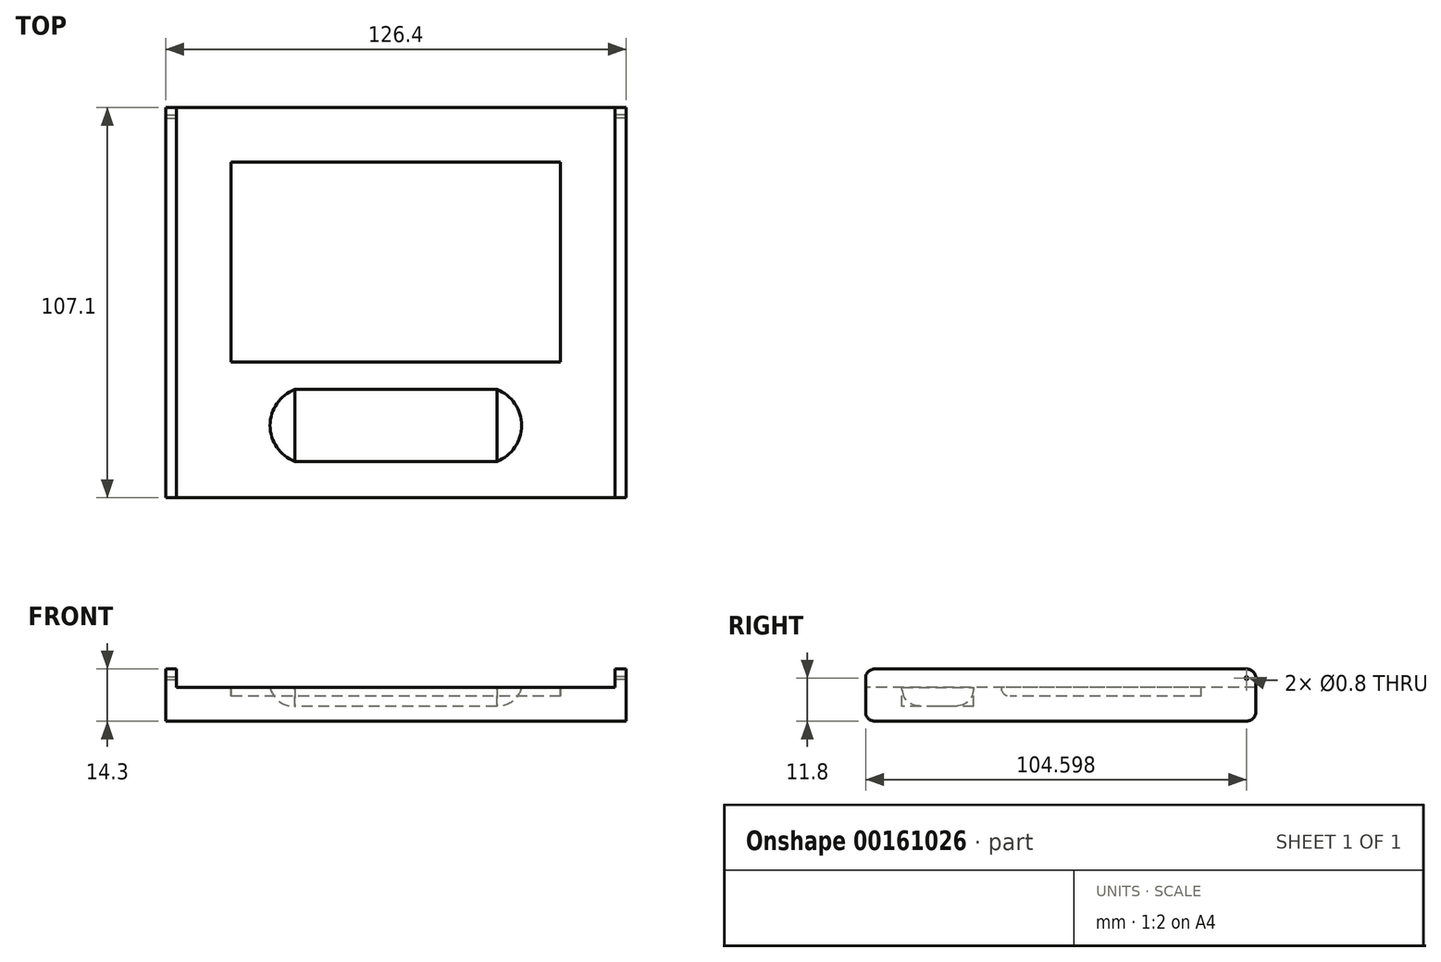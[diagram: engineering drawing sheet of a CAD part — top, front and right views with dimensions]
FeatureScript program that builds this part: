
annotation { "Feature Type Name" : "Feature", "Feature Type Description" : "" }
export const myFeature = defineFeature(function(context is Context, id is Id, definition is map)
    precondition{}
    {
        {
            var Q0;
            Q0=qCreatedBy(makeId("Top.planeOp"),FACE);
            var sketch = newSketch(context, id + "F0", { "sketchPlane" : qUnion([Q0])});
            skLineSegment(sketch, "E0", {"start": v(0, 49.02) * mm, "end": v(0, -3.38) * mm, "construction": true});
            skLineSegment(sketch, "E1.bottom", {"start": v(0, 49.02) * mm, "end": v(-45.2, 49.02) * mm});
            skLineSegment(sketch, "E1.top", {"start": v(0, -3.38) * mm, "end": v(-45.2, -3.38) * mm});
            skLineSegment(sketch, "E1.right", {"start": v(-45.2, 49.02) * mm, "end": v(-45.2, -3.38) * mm});
            skLineSegment(sketch, "E2.bottom", {"start": v(0, -13.38) * mm, "end": v(-27.75, -13.38) * mm});
            skLineSegment(sketch, "E2.top", {"start": v(-0.7, -33.08) * mm, "end": v(-27.75, -33.08) * mm});
            skLineSegment(sketch, "E2.right", {"start": v(-27.75, -13.38) * mm, "end": v(-27.75, -33.08) * mm});
            skLineSegment(sketch, "E3.bottom", {"start": v(0, 64.02) * mm, "end": v(-60.2, 64.02) * mm});
            skLineSegment(sketch, "E3.top", {"start": v(-0.7, -43.08) * mm, "end": v(-60.2, -43.08) * mm});
            skLineSegment(sketch, "E3.right", {"start": v(-60.2, 64.02) * mm, "end": v(-60.2, -43.08) * mm});
            skLineSegment(sketch, "E4.MirrorCS", {"start": v(-0.7, -43.08) * mm, "end": v(60.2, -43.08) * mm});
            skLineSegment(sketch, "E5.MirrorCS", {"start": v(-0.7, -33.08) * mm, "end": v(27.75, -33.08) * mm});
            skLineSegment(sketch, "E6.MirrorCS", {"start": v(27.75, -13.38) * mm, "end": v(27.75, -33.08) * mm});
            skLineSegment(sketch, "E7.MirrorCS", {"start": v(0, -13.38) * mm, "end": v(27.75, -13.38) * mm});
            skLineSegment(sketch, "E8.MirrorCS", {"start": v(0, -3.38) * mm, "end": v(45.2, -3.38) * mm});
            skLineSegment(sketch, "E9.MirrorCS", {"start": v(60.2, 64.02) * mm, "end": v(60.2, -43.08) * mm});
            skLineSegment(sketch, "E10.MirrorCS", {"start": v(45.2, 49.02) * mm, "end": v(45.2, -3.38) * mm});
            skLineSegment(sketch, "E11.MirrorCS", {"start": v(0, 64.02) * mm, "end": v(60.2, 64.02) * mm});
            skLineSegment(sketch, "E12.MirrorCS", {"start": v(0, 49.02) * mm, "end": v(45.2, 49.02) * mm});
            skLineSegment(sketch, "E13", {"start": v(-60.2, 64.02) * mm, "end": v(-63.2, 64.02) * mm});
            skLineSegment(sketch, "E14", {"start": v(-63.2, 64.02) * mm, "end": v(-63.2, -43.08) * mm});
            skLineSegment(sketch, "E15", {"start": v(-63.2, -43.08) * mm, "end": v(-60.2, -43.08) * mm});
            skLineSegment(sketch, "E16.MirrorCS", {"start": v(63.2, -43.08) * mm, "end": v(60.2, -43.08) * mm});
            skLineSegment(sketch, "E17.MirrorCS", {"start": v(63.2, 64.02) * mm, "end": v(63.2, -43.08) * mm});
            skLineSegment(sketch, "E18.MirrorCS", {"start": v(60.2, 64.02) * mm, "end": v(63.2, 64.02) * mm});
            skPoint(sketch, "E19.orphan", {"position": v(0.7, -33.08) * mm});
            skPoint(sketch, "E20.orphan", {"position": v(0.7, -43.08) * mm});
            skSolve(sketch);
        }
        {
            var Q0;
            Q0=makeQuery(id+"F0.imprint","IMPRINT",FACE,{"disambiguationData":[TD([[makeQuery(id+"F0.imprint","IMPRINT",EDGE,{"derivedFrom":sQuery(id+"F0.wireOp",EDGE,"E2.bottom")}),1.0]])]});
            var Q1;
            Q1=makeQuery(id+"F0.imprint","IMPRINT",FACE,{"disambiguationData":[TD([[makeQuery(id+"F0.imprint","IMPRINT",EDGE,{"derivedFrom":sQuery(id+"F0.wireOp",EDGE,"E1.bottom")}),1.0]])]});
            var Q2;
            Q2=makeQuery(id+"F0.imprint","IMPRINT",FACE,{"disambiguationData":[TD([[makeQuery(id+"F0.imprint","IMPRINT",EDGE,{"derivedFrom":sQuery(id+"F0.wireOp",EDGE,"E1.bottom")}),-1.0]])]});
            var Q3;
            Q3=makeQuery(id+"F0.imprint","IMPRINT",FACE,{"disambiguationData":[TD([[makeQuery(id+"F0.imprint","IMPRINT",EDGE,{"derivedFrom":sQuery(id+"F0.wireOp",EDGE,"E3.right")}),-1.0]])]});
            var Q4;
            Q4=makeQuery(id+"F0.imprint","IMPRINT",FACE,{"disambiguationData":[TD([[makeQuery(id+"F0.imprint","IMPRINT",EDGE,{"derivedFrom":sQuery(id+"F0.wireOp",EDGE,"E9.MirrorCS")}),1.0]])]});
            extrude(context, id + "F1", {"entities" : qUnion([Q0, Q1, Q2, Q3, Q4]), "oppositeDirection" : true, "depth" : (5 + 6.3 + 3) * mm});
        }
        {
            var Q0;
            Q0=makeQuery(id+"F0.imprint","IMPRINT",FACE,{"disambiguationData":[TD([[makeQuery(id+"F0.imprint","IMPRINT",EDGE,{"derivedFrom":sQuery(id+"F0.wireOp",EDGE,"E1.bottom")}),-1.0]])]});
            var Q1;
            Q1=makeQuery(id+"F0.imprint","IMPRINT",FACE,{"disambiguationData":[TD([[makeQuery(id+"F0.imprint","IMPRINT",EDGE,{"derivedFrom":sQuery(id+"F0.wireOp",EDGE,"E1.bottom")}),1.0]])]});
            var Q2;
            Q2=makeQuery(id+"F0.imprint","IMPRINT",FACE,{"disambiguationData":[TD([[makeQuery(id+"F0.imprint","IMPRINT",EDGE,{"derivedFrom":sQuery(id+"F0.wireOp",EDGE,"E2.bottom")}),1.0]])]});
            extrude(context, id + "F2", {"entities" : qUnion([Q0, Q1, Q2]), "operationType" : NewBodyOperationType.REMOVE, "oppositeDirection" : true, "depth" : 5 * mm});
        }
        {
            var Q0;
            Q0=makeQuery(id+"F0.imprint","IMPRINT",FACE,{"disambiguationData":[TD([[makeQuery(id+"F0.imprint","IMPRINT",EDGE,{"derivedFrom":sQuery(id+"F0.wireOp",EDGE,"E1.bottom")}),1.0]])]});
            extrude(context, id + "F3", {"entities" : qUnion([Q0]), "operationType" : NewBodyOperationType.REMOVE, "oppositeDirection" : true, "depth" : (5 + 2.5) * mm});
        }
        {
            var Q0;
            Q0=makeQuery(id+"F0.imprint","IMPRINT",FACE,{"disambiguationData":[TD([[makeQuery(id+"F0.imprint","IMPRINT",EDGE,{"derivedFrom":sQuery(id+"F0.wireOp",EDGE,"E2.bottom")}),1.0]])]});
            extrude(context, id + "F4", {"entities" : qUnion([Q0]), "operationType" : NewBodyOperationType.REMOVE, "oppositeDirection" : true, "depth" : (3 + 7.3) * mm});
        }
        {
            var Q0;
            Q0=makeQuery(id+"F2.boolean.opBoolean","COPY",FACE,{"derivedFrom":makeQuery(id+"F2.opExtrude","SWEPT_FACE",FACE,{"disambiguationData":[OSD([sQuery(id+"F0.wireOp",EDGE,"E9.MirrorCS")])]})});
            var sketch = newSketch(context, id + "F5", { "sketchPlane" : qUnion([Q0])});
            skLineSegment(sketch, "E21.0", {"start": v(-64.02, -5) * mm, "end": v(-59.02, -5) * mm, "construction": true});
            skLineSegment(sketch, "E21.1", {"start": v(-64.02, 0) * mm, "end": v(-59.02, 0) * mm, "construction": true});
            skLineSegment(sketch, "E21.2", {"start": v(-64.02, -5) * mm, "end": v(-64.02, 0) * mm, "construction": true});
            skLineSegment(sketch, "E22", {"start": v(-59.02, 0) * mm, "end": v(-59.02, -5) * mm, "construction": true});
            skPoint(sketch, "E23.end.orphan", {"position": v(43.08, 0) * mm});
            skPoint(sketch, "E24.end.orphan", {"position": v(43.08, -5) * mm});
            skLineSegment(sketch, "E25", {"start": v(-64.02, 0) * mm, "end": v(-61.52, -2.5) * mm, "construction": true});
            skLineSegment(sketch, "E26", {"start": v(-64.02, -5) * mm, "end": v(-59.02, 0) * mm, "construction": true});
            skLineSegment(sketch, "E27", {"start": v(-61.52, -2.5) * mm, "end": v(-59.02, -5) * mm, "construction": true});
            skCircle(sketch, "E28", {"center": v(-61.52, -2.5) * mm, "radius": 0.4 * mm});
            skPoint(sketch, "E28.perimeterSnap0", {"position": v(-60.27, -3.75) * mm});
            skPoint(sketch, "E28.perimeterSnap1", {"position": v(-64.02, -2.5) * mm});
            skSolve(sketch);
        }
        {
            var Q0;
            Q0=makeQuery(id+"F5.imprint","IMPRINT",FACE,{"disambiguationData":[TD([[makeQuery(id+"F5.imprint","IMPRINT",EDGE,{"derivedFrom":sQuery(id+"F5.wireOp",EDGE,"E28")}),1.0]])]});
            var Q1;
            Q1=sQuery(id+"F5.wireOp",EDGE,"E28");
            extrude(context, id + "F6", {"entities" : qUnion([Q0]), "operationType" : NewBodyOperationType.REMOVE, "surfaceEntities" : qUnion([Q1]), "endBound" : BoundingType.THROUGH_ALL, "oppositeDirection" : true, "depth" : 25 * mm});
        }
        {
            var Q0;
            Q0=makeQuery(id+"F5.imprint","IMPRINT",FACE,{"disambiguationData":[TD([[makeQuery(id+"F5.imprint","IMPRINT",EDGE,{"derivedFrom":sQuery(id+"F5.wireOp",EDGE,"E28")}),1.0]])]});
            var Q1;
            Q1=sQuery(id+"F5.wireOp",EDGE,"E28");
            extrude(context, id + "F7", {"entities" : qUnion([Q0]), "operationType" : NewBodyOperationType.REMOVE, "surfaceEntities" : qUnion([Q1]), "endBound" : BoundingType.THROUGH_ALL, "depth" : 25 * mm});
        }
        {
            var Q0;
            {var subQ0=sQuery(id+"F0.wireOp",EDGE,"E18.MirrorCS");var subQ1=sQuery(id+"F0.wireOp",EDGE,"E17.MirrorCS");var subQ2=sQuery(id+"F0.wireOp",EDGE,"E13");var subQ3=sQuery(id+"F0.wireOp",EDGE,"E11.MirrorCS");var subQ4=sQuery(id+"F0.wireOp",EDGE,"E3.bottom");Q0=makeQuery(id+"F2.boolean.opBoolean","SPLIT",EDGE,{"disambiguationData":[TD([makeQuery(id+"F1.opExtrude","SWEPT_FACE",FACE,{"disambiguationData":[OSD([subQ1])]})])],"derivedFrom":makeQuery(id+"F1.opExtrude","CAP_EDGE",EDGE,{"disambiguationData":[OSD([subQ4,subQ3,subQ2,subQ0])],"isStart":true})});}
            var Q1;
            {var subQ0=sQuery(id+"F0.wireOp",EDGE,"E18.MirrorCS");var subQ1=sQuery(id+"F0.wireOp",EDGE,"E14");var subQ2=sQuery(id+"F0.wireOp",EDGE,"E13");var subQ3=sQuery(id+"F0.wireOp",EDGE,"E11.MirrorCS");var subQ4=sQuery(id+"F0.wireOp",EDGE,"E3.bottom");Q1=makeQuery(id+"F2.boolean.opBoolean","SPLIT",EDGE,{"disambiguationData":[TD([makeQuery(id+"F1.opExtrude","SWEPT_FACE",FACE,{"disambiguationData":[OSD([subQ1])]})])],"derivedFrom":makeQuery(id+"F1.opExtrude","CAP_EDGE",EDGE,{"disambiguationData":[OSD([subQ4,subQ3,subQ2,subQ0])],"isStart":true})});}
            var Q2;
            {var subQ0=sQuery(id+"F0.wireOp",EDGE,"E17.MirrorCS");var subQ1=sQuery(id+"F0.wireOp",EDGE,"E16.MirrorCS");var subQ2=sQuery(id+"F0.wireOp",EDGE,"E15");var subQ3=sQuery(id+"F0.wireOp",EDGE,"E4.MirrorCS");var subQ4=sQuery(id+"F0.wireOp",EDGE,"E3.top");Q2=makeQuery(id+"F2.boolean.opBoolean","SPLIT",EDGE,{"disambiguationData":[TD([makeQuery(id+"F1.opExtrude","SWEPT_FACE",FACE,{"disambiguationData":[OSD([subQ0])]})])],"derivedFrom":makeQuery(id+"F1.opExtrude","CAP_EDGE",EDGE,{"disambiguationData":[OSD([subQ4,subQ3,subQ2,subQ1])],"isStart":true})});}
            var Q3;
            {var subQ0=sQuery(id+"F0.wireOp",EDGE,"E16.MirrorCS");var subQ1=sQuery(id+"F0.wireOp",EDGE,"E15");var subQ2=sQuery(id+"F0.wireOp",EDGE,"E14");var subQ3=sQuery(id+"F0.wireOp",EDGE,"E4.MirrorCS");var subQ4=sQuery(id+"F0.wireOp",EDGE,"E3.top");Q3=makeQuery(id+"F2.boolean.opBoolean","SPLIT",EDGE,{"disambiguationData":[TD([makeQuery(id+"F1.opExtrude","SWEPT_FACE",FACE,{"disambiguationData":[OSD([subQ2])]})])],"derivedFrom":makeQuery(id+"F1.opExtrude","CAP_EDGE",EDGE,{"disambiguationData":[OSD([subQ4,subQ3,subQ1,subQ0])],"isStart":true})});}
            var Q4;
            Q4=makeQuery(id+"F1.opExtrude","CAP_EDGE",EDGE,{"disambiguationData":[OSD([sQuery(id+"F0.wireOp",EDGE,"E3.bottom"),sQuery(id+"F0.wireOp",EDGE,"E11.MirrorCS"),sQuery(id+"F0.wireOp",EDGE,"E13"),sQuery(id+"F0.wireOp",EDGE,"E18.MirrorCS")])],"isStart":false});
            var Q5;
            Q5=makeQuery(id+"F1.opExtrude","CAP_EDGE",EDGE,{"disambiguationData":[OSD([sQuery(id+"F0.wireOp",EDGE,"E3.top"),sQuery(id+"F0.wireOp",EDGE,"E4.MirrorCS"),sQuery(id+"F0.wireOp",EDGE,"E15"),sQuery(id+"F0.wireOp",EDGE,"E16.MirrorCS")])],"isStart":false});
            fillet(context, id + "F8", {"entities" : qUnion([Q0, Q1, Q2, Q3, Q4, Q5]), "radius" : 2.5 * mm, "tangentPropagation" : true, "allowEdgeOverflow" : false});
        }
        {
            var Q0;
            Q0=makeQuery(id+"F2.boolean.opBoolean","COPY",FACE,{"derivedFrom":makeQuery(id+"F2.opExtrude","CAP_FACE",FACE,{"disambiguationData":[OSD([sQuery(id+"F0.wireOp",EDGE,"E3.bottom"),sQuery(id+"F0.wireOp",EDGE,"E3.top"),sQuery(id+"F0.wireOp",EDGE,"E3.right"),sQuery(id+"F0.wireOp",EDGE,"E4.MirrorCS"),sQuery(id+"F0.wireOp",EDGE,"E9.MirrorCS"),sQuery(id+"F0.wireOp",EDGE,"E11.MirrorCS")])],"isStart":false})});
            var sketch = newSketch(context, id + "F9", { "sketchPlane" : qUnion([Q0])});
            skLineSegment(sketch, "E29.0", {"start": v(-27.75, -13.38) * mm, "end": v(-27.75, -33.08) * mm, "construction": true});
            skLineSegment(sketch, "E29.1", {"start": v(27.75, -13.38) * mm, "end": v(27.75, -33.08) * mm, "construction": true});
            skLineSegment(sketch, "E29.2", {"start": v(45.2, -3.38) * mm, "end": v(-45.2, -3.38) * mm, "construction": true});
            skArc(sketch, "E30", {"start": v(-27.75, -13.38) * mm, "mid": v(-34.53, -23.23) * mm, "end": v(-27.75, -33.08) * mm});
            skPoint(sketch, "E31", {"position": v(0, -3.38) * mm});
            skLineSegment(sketch, "E32", {"start": v(0, 28.24) * mm, "end": v(0, -29.21) * mm, "construction": true});
            skArc(sketch, "E33", {"start": v(27.75, -33.08) * mm, "mid": v(34.53, -23.23) * mm, "end": v(27.75, -13.38) * mm});
            skLineSegment(sketch, "E34.0", {"start": v(45.2, -5.88) * mm, "end": v(-45.2, -5.88) * mm});
            skLineSegment(sketch, "E35", {"start": v(-45.2, -5.88) * mm, "end": v(-45.2, -3.38) * mm});
            skLineSegment(sketch, "E36", {"start": v(45.2, -3.38) * mm, "end": v(45.2, -5.88) * mm});
            skLineSegment(sketch, "E37", {"start": v(45.2, -3.38) * mm, "end": v(-45.2, -3.38) * mm});
            skSolve(sketch);
        }
        {
            var Q0;
            Q0=makeQuery(id+"F4.boolean.opBoolean","COPY",FACE,{"derivedFrom":makeQuery(id+"F4.opExtrude","SWEPT_FACE",FACE,{"disambiguationData":[OSD([sQuery(id+"F0.wireOp",EDGE,"E2.bottom"),sQuery(id+"F0.wireOp",EDGE,"E7.MirrorCS")])]})});
            var sketch = newSketch(context, id + "F10", { "sketchPlane" : qUnion([Q0])});
            skLineSegment(sketch, "E38.0", {"start": v(-27.75, -10.3) * mm, "end": v(-27.75, -5) * mm, "construction": true});
            skLineSegment(sketch, "E38.1", {"start": v(27.75, -10.3) * mm, "end": v(27.75, -5) * mm, "construction": true});
            skLineSegment(sketch, "E38.2", {"start": v(-27.75, -10.3) * mm, "end": v(27.75, -10.3) * mm, "construction": true});
            skLineSegment(sketch, "E38.3", {"start": v(-27.75, -5) * mm, "end": v(27.75, -5) * mm, "construction": true});
            skLineSegment(sketch, "E39.0", {"start": v(-27.75, -5) * mm, "end": v(-34.53, -5) * mm, "construction": true});
            skLineSegment(sketch, "E39.1", {"start": v(27.75, -5) * mm, "end": v(34.53, -5) * mm, "construction": true});
            skArc(sketch, "E40", {"start": v(-34.53, -5) * mm, "mid": v(-32.05, -8.82) * mm, "end": v(-27.75, -10.3) * mm});
            skArc(sketch, "E41", {"start": v(27.75, -10.3) * mm, "mid": v(32.05, -8.82) * mm, "end": v(34.53, -5) * mm});
            skLineSegment(sketch, "E42", {"start": v(0, -5) * mm, "end": v(0, -14.87) * mm, "construction": true});
            skPoint(sketch, "E42.endSnap0", {"position": v(0, -10.3) * mm});
            skSolve(sketch);
        }
        {
            var Q0;
            Q0=makeQuery(id+"F9.imprint","IMPRINT",FACE,{"disambiguationData":[TD([[makeQuery(id+"F9.imprint","IMPRINT",EDGE,{"derivedFrom":sQuery(id+"F9.wireOp",EDGE,"E30")}),1.0]])]});
            var Q1;
            Q1=sQuery(id+"F9.wireOp",EDGE,"E30");
            var Q2;
            Q2=sQuery(id+"F10.wireOp",EDGE,"E40");
            sweep(context, id + "F11", {"operationType" : NewBodyOperationType.REMOVE, "profiles" : qUnion([Q0]), "surfaceProfiles" : qUnion([Q1]), "path" : qUnion([Q2]), "keepProfileOrientation" : true});
        }
        {
            var Q0;
            Q0=makeQuery(id+"F9.imprint","IMPRINT",FACE,{"disambiguationData":[TD([[makeQuery(id+"F9.imprint","IMPRINT",EDGE,{"derivedFrom":sQuery(id+"F9.wireOp",EDGE,"E33")}),1.0]])]});
            var Q1;
            Q1=sQuery(id+"F10.wireOp",EDGE,"E41");
            sweep(context, id + "F12", {"operationType" : NewBodyOperationType.REMOVE, "profiles" : qUnion([Q0]), "path" : qUnion([Q1]), "keepProfileOrientation" : true});
        }
        {
            var Q0;
            Q0=makeQuery(id+"F3.boolean.opBoolean","COPY",FACE,{"derivedFrom":makeQuery(id+"F3.opExtrude","SWEPT_FACE",FACE,{"disambiguationData":[OSD([sQuery(id+"F0.wireOp",EDGE,"E1.right")])]})});
            var sketch = newSketch(context, id + "F13", { "sketchPlane" : qUnion([Q0])});
            skLineSegment(sketch, "E43.0", {"start": v(-3.38, -7.5) * mm, "end": v(-3.38, -5) * mm});
            skLineSegment(sketch, "E44.0", {"start": v(-5.88, -5) * mm, "end": v(-3.38, -5) * mm});
            skArc(sketch, "E45", {"start": v(-5.88, -5) * mm, "mid": v(-5.15, -6.77) * mm, "end": v(-3.38, -7.5) * mm});
            skSolve(sketch);
        }
        {
            var Q0;
            Q0=makeQuery(id+"F9.imprint","IMPRINT",FACE,{"disambiguationData":[TD([[makeQuery(id+"F9.imprint","IMPRINT",EDGE,{"derivedFrom":sQuery(id+"F9.wireOp",EDGE,"E34.0")}),-1.0]])]});
            var Q1;
            Q1=sQuery(id+"F13.wireOp",EDGE,"E45");
            sweep(context, id + "F14", {"operationType" : NewBodyOperationType.REMOVE, "profiles" : qUnion([Q0]), "path" : qUnion([Q1])});
        }
    });
